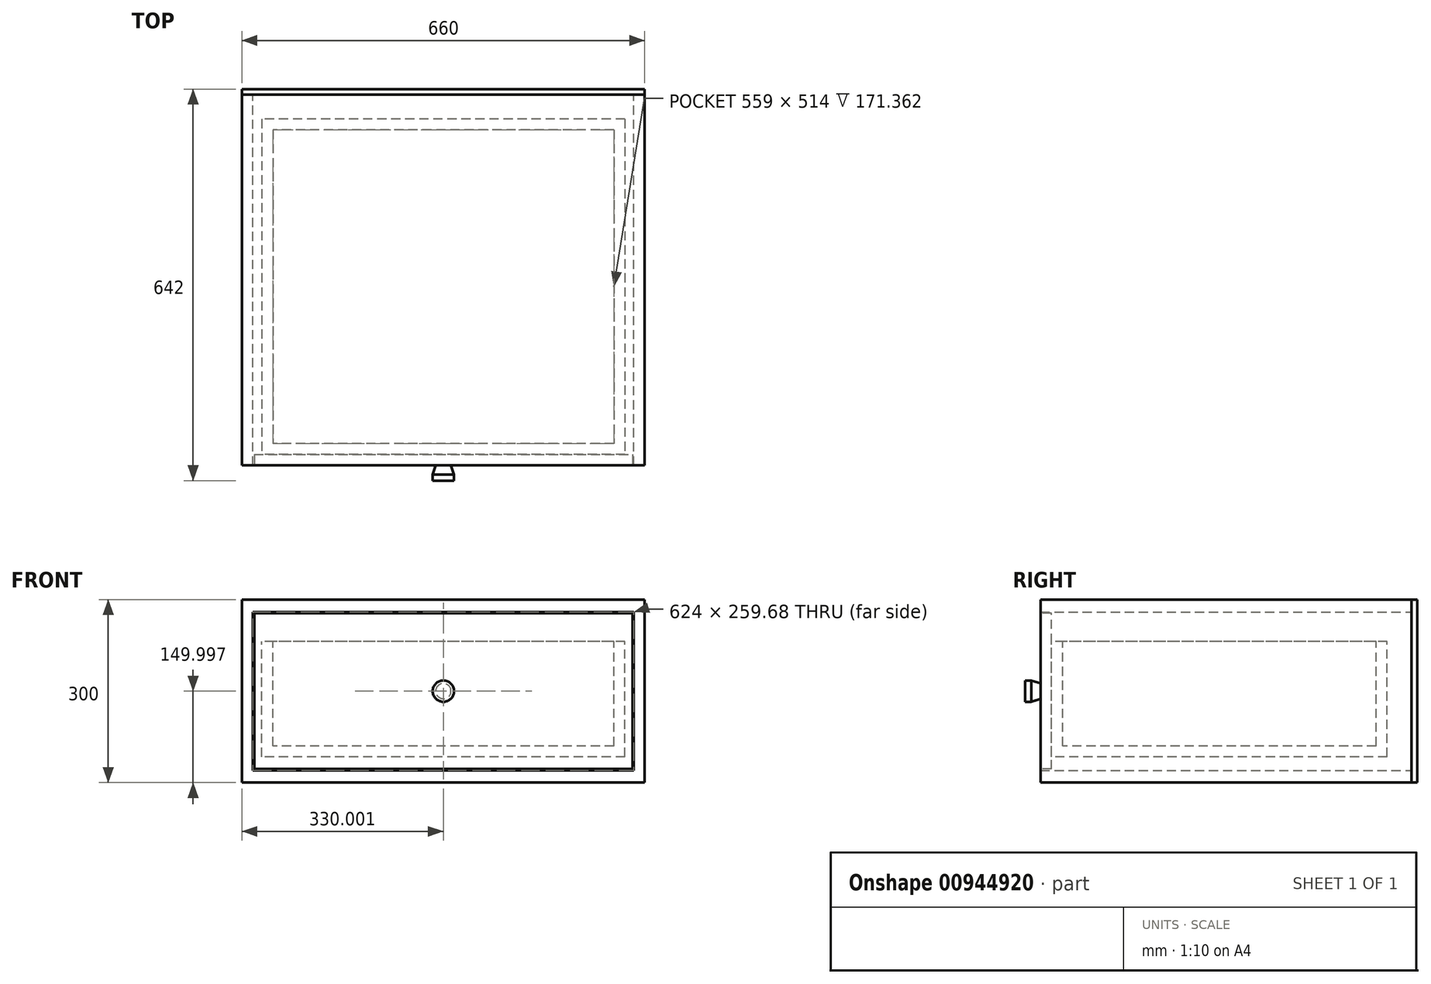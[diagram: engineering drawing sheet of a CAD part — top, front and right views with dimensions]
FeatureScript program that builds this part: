
annotation { "Feature Type Name" : "Feature", "Feature Type Description" : "" }
export const myFeature = defineFeature(function(context is Context, id is Id, definition is map)
    precondition{}
    {
        {
            var Q0;
            Q0=qCreatedBy(makeId("Front.planeOp"),FACE);
            var sketch = newSketch(context, id + "F0", { "sketchPlane" : qUnion([Q0])});
            skLineSegment(sketch, "E0", {"start": v(-326.85, -71.54) * mm, "end": v(-326.85, 228.46) * mm});
            skLineSegment(sketch, "E1.1", {"start": v(-308.85, -51.38) * mm, "end": v(-308.85, 208.3) * mm});
            skLineSegment(sketch, "E2.trimOffspring", {"start": v(315.15, -51.38) * mm, "end": v(-308.85, -51.38) * mm});
            skLineSegment(sketch, "E3.top", {"start": v(-308.85, 208.3) * mm, "end": v(315.15, 208.3) * mm});
            skLineSegment(sketch, "E4.trimOffspring", {"start": v(315.15, 208.3) * mm, "end": v(315.15, -51.38) * mm});
            skLineSegment(sketch, "E5", {"start": v(-326.85, 228.46) * mm, "end": v(333.15, 228.46) * mm});
            skLineSegment(sketch, "E6", {"start": v(333.15, -71.54) * mm, "end": v(333.15, 228.46) * mm});
            skLineSegment(sketch, "E7", {"start": v(-326.85, -71.54) * mm, "end": v(333.15, -71.54) * mm});
            skSolve(sketch);
        }
        {
            var Q0;
            Q0=qSketchRegion(id+"F0",true);
            extrude(context, id + "F1", {"entities" : qUnion([Q0]), "depth" : 608 * mm, "offsetDistance" : 25 * mm});
        }
        {
            var Q0;
            Q0=makeQuery(id+"F1.opExtrude","CAP_FACE",FACE,{"disambiguationData":[OSD([sQuery(id+"F0.wireOp",EDGE,"E0"),sQuery(id+"F0.wireOp",EDGE,"1bbb11d5-5f90-4ef2-9ceb-a32cb31813a0"),sQuery(id+"F0.wireOp",EDGE,"E1.1"),sQuery(id+"F0.wireOp",EDGE,"E2.trimOffspring"),sQuery(id+"F0.wireOp",EDGE,"E3.top"),sQuery(id+"F0.wireOp",EDGE,"E4.trimOffspring"),sQuery(id+"F0.wireOp",EDGE,"E5"),sQuery(id+"F0.wireOp",EDGE,"E6")])],"isStart":true});
            var sketch = newSketch(context, id + "F2", { "sketchPlane" : qUnion([Q0])});
            skLineSegment(sketch, "E8.left", {"start": v(-333.15, 228.46) * mm, "end": v(-333.15, 228.46) * mm});
            skLineSegment(sketch, "E8.right", {"start": v(326.85, 228.46) * mm, "end": v(326.85, 228.46) * mm});
            skLineSegment(sketch, "E9.bottom", {"start": v(-333.15, 228.46) * mm, "end": v(326.85, 228.46) * mm});
            skLineSegment(sketch, "E9.top", {"start": v(-333.15, -71.54) * mm, "end": v(326.85, -71.54) * mm});
            skLineSegment(sketch, "E9.left", {"start": v(-333.15, 228.46) * mm, "end": v(-333.15, -71.54) * mm});
            skLineSegment(sketch, "E9.right", {"start": v(326.85, 228.46) * mm, "end": v(326.85, -71.54) * mm});
            skSolve(sketch);
        }
        {
            var Q0;
            Q0=qSketchRegion(id+"F2",true);
            extrude(context, id + "F3", {"entities" : qUnion([Q0]), "depth" : 9 * mm, "offsetDistance" : 25 * mm});
        }
        {
            var Q0;
            Q0=makeQuery(id+"F1.opExtrude","CAP_FACE",FACE,{"disambiguationData":[OSD([sQuery(id+"F0.wireOp",EDGE,"E0"),sQuery(id+"F0.wireOp",EDGE,"1bbb11d5-5f90-4ef2-9ceb-a32cb31813a0"),sQuery(id+"F0.wireOp",EDGE,"E1.1"),sQuery(id+"F0.wireOp",EDGE,"E2.trimOffspring"),sQuery(id+"F0.wireOp",EDGE,"E3.top"),sQuery(id+"F0.wireOp",EDGE,"E4.trimOffspring"),sQuery(id+"F0.wireOp",EDGE,"E5"),sQuery(id+"F0.wireOp",EDGE,"E6")])],"isStart":false});
            var sketch = newSketch(context, id + "F4", { "sketchPlane" : qUnion([Q0])});
            skLineSegment(sketch, "E10.0", {"start": v(-306.85, 206.3) * mm, "end": v(313.15, 206.3) * mm});
            skLineSegment(sketch, "E10.1", {"start": v(-306.85, -49.38) * mm, "end": v(-306.85, 206.3) * mm});
            skLineSegment(sketch, "E10.2", {"start": v(313.15, -49.38) * mm, "end": v(-306.85, -49.38) * mm});
            skLineSegment(sketch, "E10.3", {"start": v(313.15, 206.3) * mm, "end": v(313.15, -49.38) * mm});
            skSolve(sketch);
        }
        {
            var Q0;
            Q0=qSketchRegion(id+"F4",true);
            extrude(context, id + "F5", {"entities" : qUnion([Q0]), "oppositeDirection" : true, "depth" : 18 * mm, "offsetDistance" : 25 * mm});
        }
        {
            var Q0;
            Q0=makeQuery(id+"F5.opExtrude","CAP_FACE",FACE,{"disambiguationData":[OSD([sQuery(id+"F4.wireOp",EDGE,"E10.0"),sQuery(id+"F4.wireOp",EDGE,"E10.1"),sQuery(id+"F4.wireOp",EDGE,"E10.2"),sQuery(id+"F4.wireOp",EDGE,"E10.3")])],"isStart":false});
            var sketch = newSketch(context, id + "F6", { "sketchPlane" : qUnion([Q0])});
            skLineSegment(sketch, "E11.bottom", {"start": v(-300.65, -29.38) * mm, "end": v(294.35, -29.38) * mm});
            skLineSegment(sketch, "E11.top", {"start": v(-300.65, 159.98) * mm, "end": v(294.35, 159.98) * mm});
            skLineSegment(sketch, "E11.left", {"start": v(-300.65, -29.38) * mm, "end": v(-300.65, 159.98) * mm});
            skLineSegment(sketch, "E11.right", {"start": v(294.35, -29.38) * mm, "end": v(294.35, 159.98) * mm});
            skSolve(sketch);
        }
        {
            var Q0;
            Q0=qSketchRegion(id+"F6",true);
            extrude(context, id + "F7", {"entities" : qUnion([Q0]), "depth" : 550 * mm, "offsetDistance" : 25 * mm});
        }
        {
            var Q0;
            Q0=makeQuery(id+"F7.opExtrude","SWEPT_FACE",FACE,{"disambiguationData":[OSD([sQuery(id+"F6.wireOp",EDGE,"E11.top")])]});
            shell(context, id + "F8", {"entities" : qUnion([Q0]), "thickness" : 18 * mm});
        }
        {
            var Q0;
            Q0=makeQuery(id+"F5.opExtrude","CAP_FACE",FACE,{"disambiguationData":[OSD([sQuery(id+"F4.wireOp",EDGE,"E10.0"),sQuery(id+"F4.wireOp",EDGE,"E10.1"),sQuery(id+"F4.wireOp",EDGE,"E10.2"),sQuery(id+"F4.wireOp",EDGE,"E10.3")])],"isStart":true});
            var sketch = newSketch(context, id + "F9", { "sketchPlane" : qUnion([Q0])});
            skLineSegment(sketch, "E12", {"start": v(313.15, 78.46) * mm, "end": v(-306.85, 78.46) * mm, "construction": true});
            skCircle(sketch, "E13", {"center": v(3.15, 78.46) * mm, "radius": 17.5 * mm});
            skSolve(sketch);
        }
        {
            var Q0;
            Q0 = qSketchRegion(id + "F9", true);
            extrude(context, id + "F10", {"entities" : qUnion([Q0]), "depth" : 25 * mm, "offsetDistance" : 25 * mm});
        }
        {
            var Q0;
            Q0=makeQuery(id+"F10.opExtrude","CAP_EDGE",EDGE,{"disambiguationData":[OSD([sQuery(id+"F9.wireOp",EDGE,"E13")])],"isStart":true});
            chamfer(context, id + "F11", {"entities" : qUnion([Q0]), "chamferType" : ChamferType.TWO_OFFSETS, "width1" : 15 * mm, "oppositeDirection" : false, "width2" : 5 * mm, "tangentPropagation" : true});
        }
    });
